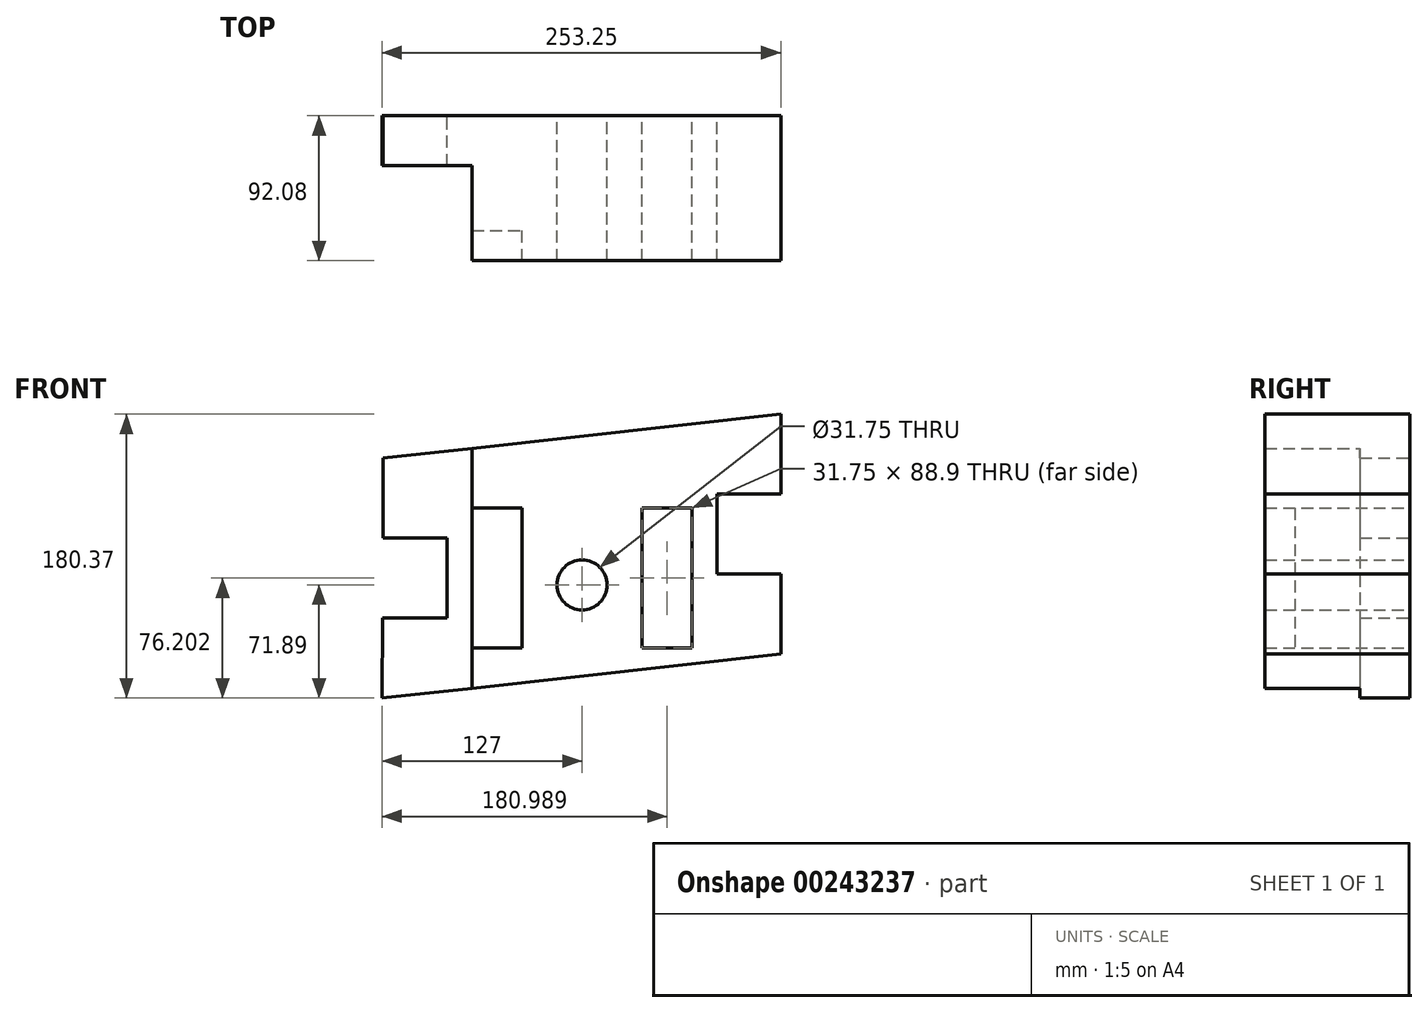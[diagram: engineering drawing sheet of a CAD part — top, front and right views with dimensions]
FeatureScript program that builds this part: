
annotation { "Feature Type Name" : "Feature", "Feature Type Description" : "" }
export const myFeature = defineFeature(function(context is Context, id is Id, definition is map)
    precondition{}
    {
        {
            var Q0;
            Q0=qCreatedBy(makeId("Front.planeOp"),FACE);
            var sketch = newSketch(context, id + "F0", { "sketchPlane" : qUnion([Q0])});
            skLineSegment(sketch, "E0.left", {"start": v(-126.22, 80.6) * mm, "end": v(-126.48, 29.71) * mm});
            skLineSegment(sketch, "E0.right", {"start": v(126.25, 108.48) * mm, "end": v(126.25, 57.68) * mm});
            skCircle(sketch, "E1", {"center": v(0, 0) * mm, "radius": 15.88 * mm});
            skLineSegment(sketch, "E2.bottom", {"start": v(-126.48, 29.71) * mm, "end": v(-85.72, 29.71) * mm});
            skLineSegment(sketch, "E2.top", {"start": v(-126.74, -21.09) * mm, "end": v(-85.72, -21.09) * mm});
            skLineSegment(sketch, "E2.right", {"start": v(-85.72, 29.71) * mm, "end": v(-85.72, -21.09) * mm});
            skLineSegment(sketch, "E3.trimOffspring", {"start": v(-126.74, -21.09) * mm, "end": v(-127, -71.89) * mm});
            skLineSegment(sketch, "E4.bottom", {"start": v(85.72, 57.68) * mm, "end": v(126.25, 57.68) * mm});
            skLineSegment(sketch, "E4.top", {"start": v(85.73, 6.88) * mm, "end": v(126.25, 6.88) * mm});
            skLineSegment(sketch, "E4.left", {"start": v(85.72, 57.68) * mm, "end": v(85.72, 6.88) * mm});
            skLineSegment(sketch, "E5.trimOffspring", {"start": v(126.25, 6.88) * mm, "end": v(126.25, -43.92) * mm});
            skLineSegment(sketch, "E6.top", {"start": v(-69.84, 48.76) * mm, "end": v(-38.09, 48.76) * mm});
            skLineSegment(sketch, "E6.right", {"start": v(-38.09, 80.51) * mm, "end": v(-38.09, 48.76) * mm});
            skLineSegment(sketch, "E7.top", {"start": v(38.11, 48.76) * mm, "end": v(69.86, 48.76) * mm});
            skLineSegment(sketch, "E7.left", {"start": v(38.11, 80.51) * mm, "end": v(38.11, 48.76) * mm});
            skLineSegment(sketch, "E7.right", {"start": v(69.86, 80.51) * mm, "end": v(69.86, 48.76) * mm});
            skLineSegment(sketch, "E8.bottom", {"start": v(38.11, -40.14) * mm, "end": v(69.86, -40.14) * mm});
            skLineSegment(sketch, "E8.left", {"start": v(38.11, -40.14) * mm, "end": v(38.11, -71.89) * mm});
            skLineSegment(sketch, "E8.right", {"start": v(69.86, -40.14) * mm, "end": v(69.86, -71.89) * mm});
            skLineSegment(sketch, "E9.bottom", {"start": v(-69.84, -40.14) * mm, "end": v(-38.09, -40.14) * mm});
            skLineSegment(sketch, "E9.right", {"start": v(-38.09, -40.14) * mm, "end": v(-38.09, -71.89) * mm});
            skLineSegment(sketch, "E10.right", {"start": v(-38.09, 48.76) * mm, "end": v(-38.09, -40.14) * mm});
            skLineSegment(sketch, "E11.left", {"start": v(38.11, 48.76) * mm, "end": v(38.11, -40.14) * mm});
            skLineSegment(sketch, "E11.right", {"start": v(69.86, 48.76) * mm, "end": v(69.86, -40.14) * mm});
            skLineSegment(sketch, "E12", {"start": v(-126.22, 80.6) * mm, "end": v(126.25, 108.48) * mm});
            skLineSegment(sketch, "E13", {"start": v(-127, -71.89) * mm, "end": v(126.25, -43.92) * mm});
            skLineSegment(sketch, "E14", {"start": v(-69.84, 86.83) * mm, "end": v(-69.84, -65.57) * mm});
            skSolve(sketch);
        }
        {
            var Q0;
            Q0=makeQuery(id+"F0.imprint","IMPRINT",FACE,{"disambiguationData":[TD([[makeQuery(id+"F0.imprint","IMPRINT",EDGE,{"derivedFrom":sQuery(id+"F0.wireOp",EDGE,"E0.left")}),1.0]])]});
            var Q1;
            Q1=makeQuery(id+"F0.imprint","IMPRINT",FACE,{"disambiguationData":[TD([[makeQuery(id+"F0.imprint","IMPRINT",EDGE,{"derivedFrom":sQuery(id+"F0.wireOp",EDGE,"E6.top")}),1.0]])]});
            var Q2;
            Q2=makeQuery(id+"F0.imprint","IMPRINT",FACE,{"disambiguationData":[TD([[makeQuery(id+"F0.imprint","IMPRINT",EDGE,{"derivedFrom":sQuery(id+"F0.wireOp",EDGE,"E10.bottom")}),-1.0]])]});
            var Q3;
            Q3=makeQuery(id+"F0.imprint","IMPRINT",FACE,{"disambiguationData":[TD([[makeQuery(id+"F0.imprint","IMPRINT",EDGE,{"derivedFrom":sQuery(id+"F0.wireOp",EDGE,"E9.bottom")}),-1.0]])]});
            var Q4;
            Q4=makeQuery(id+"F0.imprint","IMPRINT",FACE,{"disambiguationData":[TD([[makeQuery(id+"F0.imprint","IMPRINT",EDGE,{"derivedFrom":sQuery(id+"F0.wireOp",EDGE,"E1")}),-1.0]])]});
            var Q5;
            Q5=makeQuery(id+"F0.imprint","IMPRINT",FACE,{"disambiguationData":[TD([[makeQuery(id+"F0.imprint","IMPRINT",EDGE,{"derivedFrom":sQuery(id+"F0.wireOp",EDGE,"E11.bottom")}),-1.0]])]});
            var Q6;
            Q6=makeQuery(id+"F0.imprint","IMPRINT",FACE,{"disambiguationData":[TD([[makeQuery(id+"F0.imprint","IMPRINT",EDGE,{"derivedFrom":sQuery(id+"F0.wireOp",EDGE,"E8.top")}),1.0]])]});
            var Q7;
            Q7=makeQuery(id+"F0.imprint","IMPRINT",FACE,{"disambiguationData":[TD([[makeQuery(id+"F0.imprint","IMPRINT",EDGE,{"derivedFrom":sQuery(id+"F0.wireOp",EDGE,"E0.right")}),-1.0]])]});
            var Q8;
            Q8=makeQuery(id+"F0.imprint","IMPRINT",FACE,{"disambiguationData":[TD([[makeQuery(id+"F0.imprint","IMPRINT",EDGE,{"derivedFrom":sQuery(id+"F0.wireOp",EDGE,"E7.left")}),1.0]])]});
            extrude(context, id + "F1", {"entities" : qUnion([Q0, Q1, Q2, Q3, Q4, Q5, Q6, Q7, Q8]), "depth" : 31.75 * mm});
        }
        {
            var Q0;
            {var subQ0=sQuery(id+"F0.wireOp",EDGE,"E6.top");Q0=makeQuery(id+"F0.imprint","IMPRINT",FACE,{"disambiguationData":[TD([[makeQuery(id+"F0.imprint","IMPRINT",EDGE,{"derivedFrom":subQ0}),1.0]])]});}
            var Q1;
            {var subQ0=sQuery(id+"F0.wireOp",EDGE,"E9.right");Q1=makeQuery(id+"F0.imprint","IMPRINT",FACE,{"disambiguationData":[TD([[makeQuery(id+"F0.imprint","IMPRINT",EDGE,{"derivedFrom":subQ0}),-1.0]])]});}
            var Q2;
            {var subQ0=sQuery(id+"F0.wireOp",EDGE,"E8.left");Q2=makeQuery(id+"F0.imprint","IMPRINT",FACE,{"disambiguationData":[TD([[makeQuery(id+"F0.imprint","IMPRINT",EDGE,{"derivedFrom":subQ0}),1.0]])]});}
            var Q3;
            {var subQ0=sQuery(id+"F0.wireOp",EDGE,"E7.left");Q3=makeQuery(id+"F0.imprint","IMPRINT",FACE,{"disambiguationData":[TD([[makeQuery(id+"F0.imprint","IMPRINT",EDGE,{"derivedFrom":subQ0}),1.0]])]});}
            extrude(context, id + "F2", {"entities" : qUnion([Q0, Q1, Q2, Q3]), "operationType" : NewBodyOperationType.ADD, "depth" : 92.07 * mm});
        }
        {
            var Q0;
            {var subQ0=sQuery(id+"F0.wireOp",EDGE,"E6.top");Q0=makeQuery(id+"F0.imprint","IMPRINT",FACE,{"disambiguationData":[TD([[makeQuery(id+"F0.imprint","IMPRINT",EDGE,{"derivedFrom":subQ0}),-1.0]])]});}
            var Q1;
            Q1=makeQuery(id+"F0.imprint","IMPRINT",FACE,{"disambiguationData":[TD([[makeQuery(id+"F0.imprint","IMPRINT",EDGE,{"derivedFrom":sQuery(id+"F0.wireOp",EDGE,"E11.bottom")}),-1.0]])]});
            extrude(context, id + "F3", {"entities" : qUnion([Q0, Q1]), "operationType" : NewBodyOperationType.ADD, "depth" : 73.02 * mm});
        }
        {
            var Q0;
            Q0=makeQuery(id+"F0.imprint","IMPRINT",FACE,{"disambiguationData":[TD([[makeQuery(id+"F0.imprint","IMPRINT",EDGE,{"derivedFrom":sQuery(id+"F0.wireOp",EDGE,"E1")}),-1.0]])]});
            extrude(context, id + "F4", {"entities" : qUnion([Q0]), "operationType" : NewBodyOperationType.ADD, "depth" : 53.97 * mm});
        }
    });
